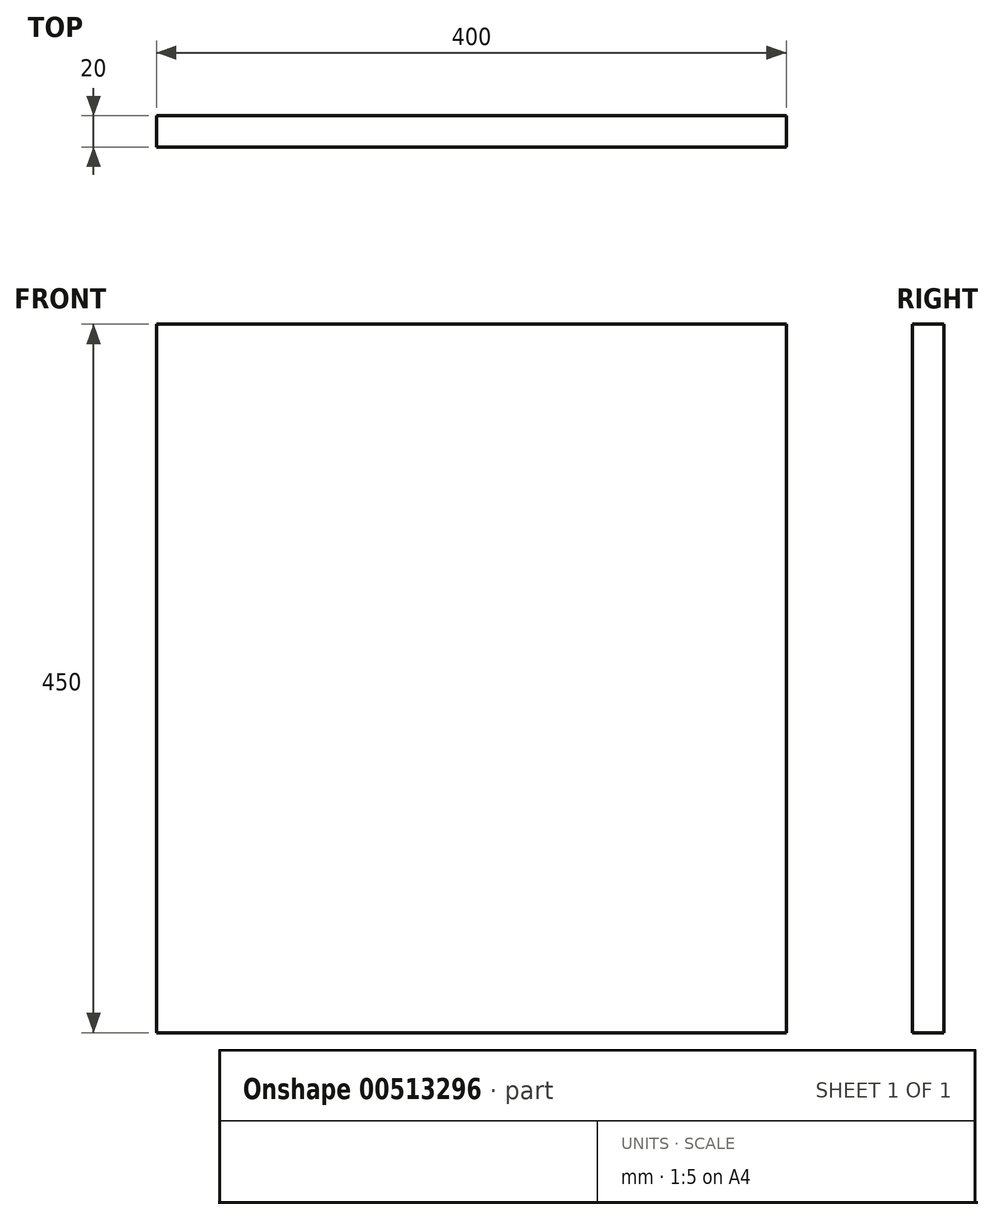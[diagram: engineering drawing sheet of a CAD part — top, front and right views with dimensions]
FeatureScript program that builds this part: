
annotation { "Feature Type Name" : "Feature", "Feature Type Description" : "" }
export const myFeature = defineFeature(function(context is Context, id is Id, definition is map)
    precondition{}
    {
        {
            var Q0;
            Q0=qCreatedBy(makeId("Front.planeOp"),FACE);
            var sketch = newSketch(context, id + "F0", { "sketchPlane" : qUnion([Q0])});
            skLineSegment(sketch, "E0.bottom", {"start": v(-200, 225) * mm, "end": v(200, 225) * mm});
            skLineSegment(sketch, "E0.top", {"start": v(-200, -225) * mm, "end": v(200, -225) * mm});
            skLineSegment(sketch, "E0.left", {"start": v(-200, 225) * mm, "end": v(-200, -225) * mm});
            skLineSegment(sketch, "E0.right", {"start": v(200, 225) * mm, "end": v(200, -225) * mm});
            skPoint(sketch, "E0.middle", {"position": v(0, 0) * mm});
            skSolve(sketch);
        }
        {
            var Q0;
            Q0 = qSketchRegion(id + "F0", true);
            extrude(context, id + "F1", {"entities" : qUnion([Q0]), "depth" : 20 * mm, "offsetDistance" : 25 * mm});
        }
    });
